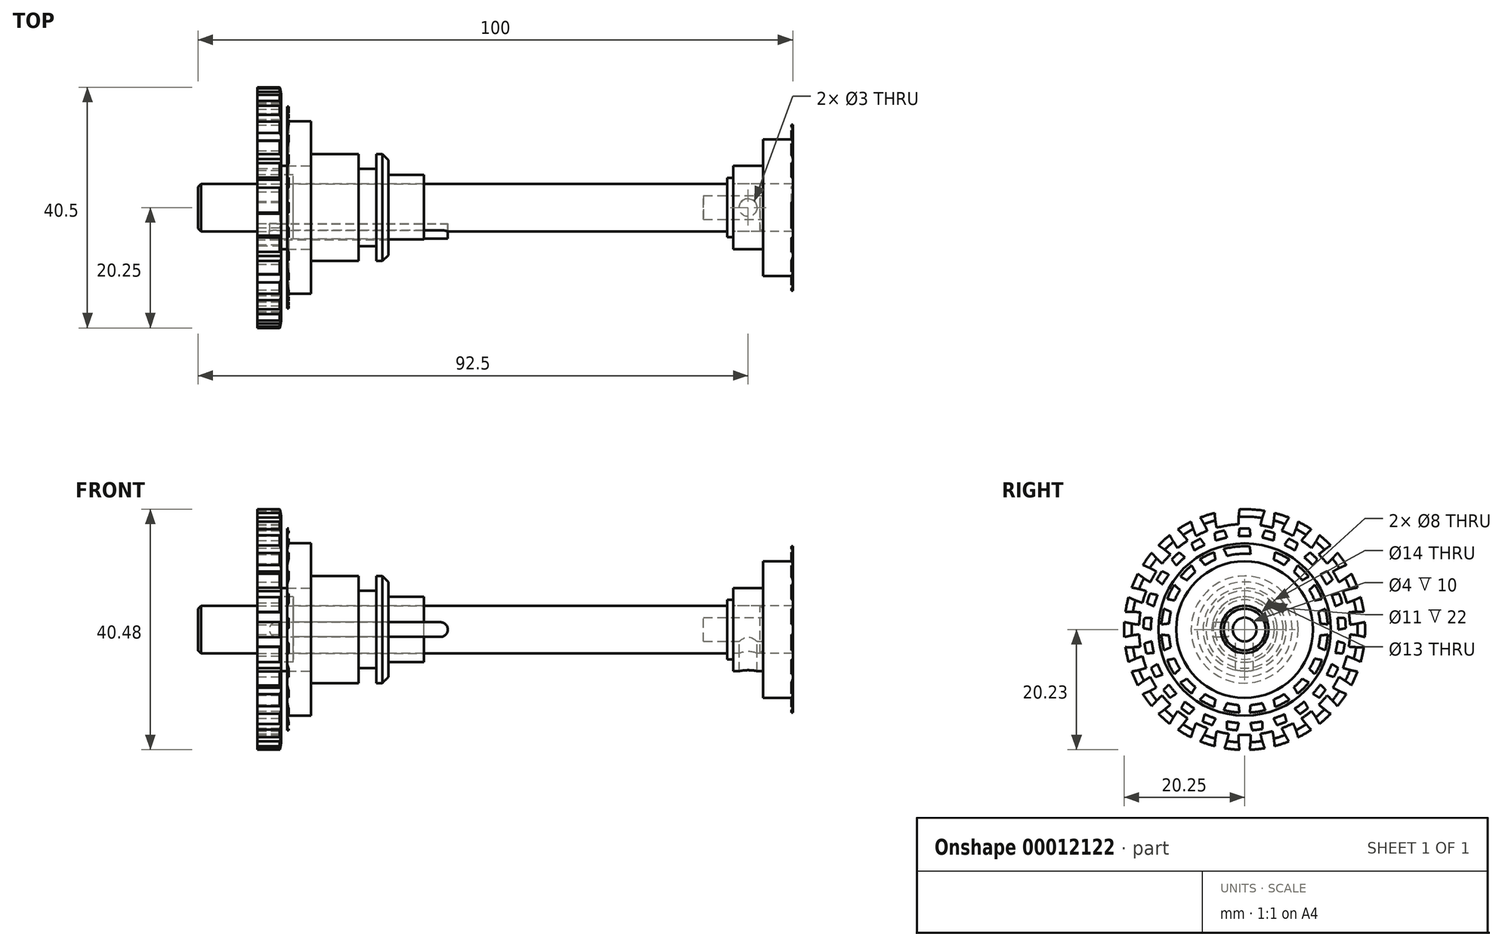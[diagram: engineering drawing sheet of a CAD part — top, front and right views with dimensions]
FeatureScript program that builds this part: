
annotation { "Feature Type Name" : "Feature", "Feature Type Description" : "" }
export const myFeature = defineFeature(function(context is Context, id is Id, definition is map)
    precondition{}
    {
        {
            var Q0;
            Q0=qCreatedBy(makeId("Right.planeOp"),FACE);
            var sketch = newSketch(context, id + "F0", { "sketchPlane" : qUnion([Q0])});
            skCircle(sketch, "E0", {"center": v(0, 0) * mm, "radius": 2 * mm});
            skCircle(sketch, "E1", {"center": v(0, 0) * mm, "radius": 4 * mm});
            skCircle(sketch, "E2", {"center": v(0, 0) * mm, "radius": 5 * mm});
            skSolve(sketch);
        }
        {
            var Q0;
            Q0=makeQuery(id+"F0.imprint","IMPRINT",FACE,{"disambiguationData":[TD([[makeQuery(id+"F0.imprint","IMPRINT",EDGE,{"derivedFrom":sQuery(id+"F0.wireOp",EDGE,"E0")}),-1.0]])]});
            var Q1;
            Q1=makeQuery(id+"F0.imprint","IMPRINT",FACE,{"disambiguationData":[TD([[makeQuery(id+"F0.imprint","IMPRINT",EDGE,{"derivedFrom":sQuery(id+"F0.wireOp",EDGE,"E0")}),1.0]])]});
            extrude(context, id + "F1", {"entities" : qUnion([Q0, Q1]), "oppositeDirection" : true, "depth" : 90 * mm});
        }
        {
            var Q0;
            Q0=makeQuery(id+"F0.imprint","IMPRINT",FACE,{"disambiguationData":[TD([[makeQuery(id+"F0.imprint","IMPRINT",EDGE,{"derivedFrom":sQuery(id+"F0.wireOp",EDGE,"E1")}),-1.0]])]});
            var Q1;
            Q1=makeQuery(id+"F0.imprint","IMPRINT",FACE,{"disambiguationData":[TD([[makeQuery(id+"F0.imprint","IMPRINT",EDGE,{"derivedFrom":sQuery(id+"F0.wireOp",EDGE,"E0")}),-1.0]])]});
            extrude(context, id + "F2", {"entities" : qUnion([Q0, Q1]), "operationType" : NewBodyOperationType.ADD, "oppositeDirection" : true, "depth" : 1 * mm});
        }
        {
            var Q0;
            Q0=makeQuery(id+"F0.imprint","IMPRINT",FACE,{"disambiguationData":[TD([[makeQuery(id+"F0.imprint","IMPRINT",EDGE,{"derivedFrom":sQuery(id+"F0.wireOp",EDGE,"E0")}),1.0]])]});
            extrude(context, id + "F3", {"entities" : qUnion([Q0]), "operationType" : NewBodyOperationType.REMOVE, "oppositeDirection" : true, "depth" : 5 * mm});
        }
        {
            var Q0;
            Q0=makeQuery(id+"F0.imprint","IMPRINT",FACE,{"disambiguationData":[TD([[makeQuery(id+"F0.imprint","IMPRINT",EDGE,{"derivedFrom":sQuery(id+"F0.wireOp",EDGE,"E0")}),-1.0]])]});
            extrude(context, id + "F4", {"entities" : qUnion([Q0]), "operationType" : NewBodyOperationType.ADD, "depth" : 5 * mm});
        }
        {
            var Q0;
            Q0=qCreatedBy(makeId("Front.planeOp"),FACE);
            cPlane(context, id + "F5", {"entities" : qUnion([Q0]), "cplaneType" : CPlaneType.OFFSET, "offset" : 4 * mm, "width" : 150 * mm, "height" : 150 * mm});
        }
        {
            var Q0;
            Q0=qCreatedBy(id+"F5.planeOp",FACE);
            var sketch = newSketch(context, id + "F6", { "sketchPlane" : qUnion([Q0])});
            skLineSegment(sketch, "E3.0", {"start": v(-90, 4) * mm, "end": v(-90, -4) * mm});
            skLineSegment(sketch, "E4", {"start": v(-90, 0) * mm, "end": v(-49.25, 0) * mm, "construction": true});
            skCircle(sketch, "E5", {"center": v(-49.25, 0) * mm, "radius": 1.25 * mm});
            skCircle(sketch, "E6", {"center": v(-76.75, 0) * mm, "radius": 1.25 * mm});
            skLineSegment(sketch, "E7", {"start": v(-76.75, 1.25) * mm, "end": v(-49.25, 1.25) * mm});
            skLineSegment(sketch, "E8", {"start": v(-76.75, -1.25) * mm, "end": v(-49.25, -1.25) * mm});
            skSolve(sketch);
        }
        {
            var Q0;
            {var subQ0=sQuery(id+"F6.wireOp",EDGE,"E6");var subQ2=makeQuery(id+"F6.imprint","INTERSECT",VERTEX,{"derivedFrom":[subQ0,sQuery(id+"F6.wireOp",EDGE,"E7")]});Q0=makeQuery(id+"F6.imprint","IMPRINT",FACE,{"disambiguationData":[TD([[makeQuery(id+"F6.imprint","IMPRINT",EDGE,{"disambiguationData":[TD([[subQ2,-1.0]])],"derivedFrom":subQ0}),1.0]])]});}
            var Q1;
            {var subQ1=sQuery(id+"F6.wireOp",EDGE,"E7");Q1=makeQuery(id+"F6.imprint","IMPRINT",FACE,{"disambiguationData":[TD([[makeQuery(id+"F6.imprint","IMPRINT",EDGE,{"derivedFrom":subQ1}),-1.0]])]});}
            var Q2;
            {var subQ0=sQuery(id+"F6.wireOp",EDGE,"E5");var subQ2=makeQuery(id+"F6.imprint","INTERSECT",VERTEX,{"derivedFrom":[subQ0,sQuery(id+"F6.wireOp",EDGE,"E7")]});Q2=makeQuery(id+"F6.imprint","IMPRINT",FACE,{"disambiguationData":[TD([[makeQuery(id+"F6.imprint","IMPRINT",EDGE,{"disambiguationData":[TD([[subQ2,-1.0]])],"derivedFrom":subQ0}),1.0]])]});}
            extrude(context, id + "F7", {"entities" : qUnion([Q0, Q1, Q2]), "operationType" : NewBodyOperationType.REMOVE, "oppositeDirection" : true, "depth" : 1.3 * mm});
        }
        {
            var Q0;
            {var subQ0=sQuery(id+"F6.wireOp",EDGE,"E6");var subQ2=makeQuery(id+"F6.imprint","INTERSECT",VERTEX,{"derivedFrom":[subQ0,sQuery(id+"F6.wireOp",EDGE,"E7")]});Q0=makeQuery(id+"F6.imprint","IMPRINT",FACE,{"disambiguationData":[TD([[makeQuery(id+"F6.imprint","IMPRINT",EDGE,{"disambiguationData":[TD([[subQ2,-1.0]])],"derivedFrom":subQ0}),1.0]])]});}
            var Q1;
            {var subQ1=sQuery(id+"F6.wireOp",EDGE,"E7");Q1=makeQuery(id+"F6.imprint","IMPRINT",FACE,{"disambiguationData":[TD([[makeQuery(id+"F6.imprint","IMPRINT",EDGE,{"derivedFrom":subQ1}),-1.0]])]});}
            var Q2;
            {var subQ0=sQuery(id+"F6.wireOp",EDGE,"E5");var subQ2=makeQuery(id+"F6.imprint","INTERSECT",VERTEX,{"derivedFrom":[subQ0,sQuery(id+"F6.wireOp",EDGE,"E7")]});Q2=makeQuery(id+"F6.imprint","IMPRINT",FACE,{"disambiguationData":[TD([[makeQuery(id+"F6.imprint","IMPRINT",EDGE,{"disambiguationData":[TD([[subQ2,-1.0]])],"derivedFrom":subQ0}),1.0]])]});}
            extrude(context, id + "F8", {"entities" : qUnion([Q0, Q1, Q2]), "depth" : 2.5 * mm, "symmetric" : true});
        }
        {
            var Q0;
            Q0=makeQuery(id+"F4.opExtrude","CAP_EDGE",EDGE,{"disambiguationData":[OSD([sQuery(id+"F0.wireOp",EDGE,"E1")])],"isStart":false});
            var Q1;
            Q1=makeQuery(id+"F1.opExtrude","CAP_EDGE",EDGE,{"disambiguationData":[OSD([sQuery(id+"F0.wireOp",EDGE,"E1")])],"isStart":false});
            chamfer(context, id + "F9", {"entities" : qUnion([Q0, Q1]), "width" : 0.5 * mm, "tangentPropagation" : true});
        }
        {
            var Q0;
            Q0=qCreatedBy(makeId("Right.planeOp"),FACE);
            cPlane(context, id + "F10", {"entities" : qUnion([Q0]), "cplaneType" : CPlaneType.OFFSET, "offset" : (48 + 15) * mm, "oppositeDirection" : true, "width" : 150 * mm, "height" : 150 * mm});
        }
        {
            var Q0;
            Q0=qCreatedBy(id+"F10.planeOp",FACE);
            var sketch = newSketch(context, id + "F11", { "sketchPlane" : qUnion([Q0])});
            skCircle(sketch, "E9.0", {"center": v(0, 0) * mm, "radius": 4 * mm});
            skLineSegment(sketch, "E9.1", {"start": v(-5.36, -1.25) * mm, "end": v(-2.75, -1.25) * mm});
            skLineSegment(sketch, "E9.2", {"start": v(-5.36, 1.25) * mm, "end": v(-2.75, 1.25) * mm});
            skCircle(sketch, "E10", {"center": v(0, 0) * mm, "radius": 5.5 * mm});
            skPoint(sketch, "E11.orphan", {"position": v(-5.25, 1.25) * mm});
            skPoint(sketch, "E12.orphan", {"position": v(-5.25, -1.25) * mm});
            skSolve(sketch);
        }
        {
            var Q0;
            {var subQ3=sQuery(id+"F11.wireOp",EDGE,"E9.1");var subQ5=sQuery(id+"F11.wireOp",EDGE,"E9.0");var subQ7=makeQuery(id+"F11.imprint","INTERSECT",VERTEX,{"derivedFrom":[subQ5,subQ3]});Q0=makeQuery(id+"F11.imprint","IMPRINT",FACE,{"disambiguationData":[TD([[makeQuery(id+"F11.imprint","IMPRINT",EDGE,{"disambiguationData":[TD([[subQ7,-1.0]])],"derivedFrom":subQ5}),-1.0]])]});}
            extrude(context, id + "F12", {"entities" : qUnion([Q0]), "depth" : 22 * mm, "symmetric" : true});
        }
        {
            var Q0;
            Q0=qCreatedBy(id+"F10.planeOp",FACE);
            var sketch = newSketch(context, id + "F13", { "sketchPlane" : qUnion([Q0])});
            skCircle(sketch, "E13.1", {"center": v(0, 0) * mm, "radius": 5.5 * mm});
            skCircle(sketch, "E14", {"center": v(0, 0) * mm, "radius": 6.5 * mm});
            skCircle(sketch, "E15", {"center": v(0, 0) * mm, "radius": 7 * mm});
            skCircle(sketch, "E16", {"center": v(0, 0) * mm, "radius": 9 * mm});
            skSolve(sketch);
        }
        {
            var Q0;
            Q0=makeQuery(id+"F13.imprint","IMPRINT",FACE,{"disambiguationData":[TD([[makeQuery(id+"F13.imprint","IMPRINT",EDGE,{"derivedFrom":sQuery(id+"F13.wireOp",EDGE,"E13.1")}),-1.0]])]});
            var Q1;
            Q1=makeQuery(id+"F13.imprint","IMPRINT",FACE,{"disambiguationData":[TD([[makeQuery(id+"F13.imprint","IMPRINT",EDGE,{"derivedFrom":sQuery(id+"F13.wireOp",EDGE,"E14")}),-1.0]])]});
            var Q2;
            Q2=makeQuery(id+"F13.imprint","IMPRINT",FACE,{"disambiguationData":[TD([[makeQuery(id+"F13.imprint","IMPRINT",EDGE,{"derivedFrom":sQuery(id+"F13.wireOp",EDGE,"E15")}),-1.0]])]});
            extrude(context, id + "F14", {"entities" : qUnion([Q0, Q1, Q2]), "depth" : 5 * mm});
        }
        {
            var Q0;
            Q0=makeQuery(id+"F13.imprint","IMPRINT",FACE,{"disambiguationData":[TD([[makeQuery(id+"F13.imprint","IMPRINT",EDGE,{"derivedFrom":sQuery(id+"F13.wireOp",EDGE,"E15")}),-1.0]])]});
            var Q1;
            Q1=makeQuery(id+"F13.imprint","IMPRINT",FACE,{"disambiguationData":[TD([[makeQuery(id+"F13.imprint","IMPRINT",EDGE,{"derivedFrom":sQuery(id+"F13.wireOp",EDGE,"E14")}),-1.0]])]});
            extrude(context, id + "F15", {"entities" : qUnion([Q0, Q1]), "operationType" : NewBodyOperationType.REMOVE, "depth" : 3 * mm});
        }
        {
            var Q0;
            Q0=makeQuery(id+"F13.imprint","IMPRINT",FACE,{"disambiguationData":[TD([[makeQuery(id+"F13.imprint","IMPRINT",EDGE,{"derivedFrom":sQuery(id+"F13.wireOp",EDGE,"E13.1")}),-1.0]])]});
            extrude(context, id + "F16", {"entities" : qUnion([Q0]), "operationType" : NewBodyOperationType.ADD, "oppositeDirection" : true, "depth" : (4 + 5 + 8) * mm});
        }
        {
            var Q0;
            Q0=makeQuery(id+"F13.imprint","IMPRINT",FACE,{"disambiguationData":[TD([[makeQuery(id+"F13.imprint","IMPRINT",EDGE,{"derivedFrom":sQuery(id+"F13.wireOp",EDGE,"E14")}),-1.0]])]});
            extrude(context, id + "F17", {"entities" : qUnion([Q0]), "operationType" : NewBodyOperationType.ADD, "oppositeDirection" : true, "depth" : (5 + 8) * mm});
        }
        {
            var Q0;
            Q0=makeQuery(id+"F13.imprint","IMPRINT",FACE,{"disambiguationData":[TD([[makeQuery(id+"F13.imprint","IMPRINT",EDGE,{"derivedFrom":sQuery(id+"F13.wireOp",EDGE,"E15")}),-1.0]])]});
            extrude(context, id + "F18", {"entities" : qUnion([Q0]), "operationType" : NewBodyOperationType.ADD, "oppositeDirection" : true, "depth" : 8 * mm});
        }
        {
            var Q0;
            Q0=makeQuery(id+"F14.opExtrude","CAP_EDGE",EDGE,{"disambiguationData":[OSD([sQuery(id+"F13.wireOp",EDGE,"E16")])],"isStart":false});
            chamfer(context, id + "F19", {"entities" : qUnion([Q0]), "width" : 1 * mm, "tangentPropagation" : true});
        }
        {
            var Q0;
            Q0=makeQuery(id+"F17.opExtrude","CAP_FACE",FACE,{"disambiguationData":[OSD([sQuery(id+"F13.wireOp",EDGE,"E14"),sQuery(id+"F13.wireOp",EDGE,"E15")])],"isStart":false});
            var sketch = newSketch(context, id + "F20", { "sketchPlane" : qUnion([Q0])});
            skCircle(sketch, "E17.0", {"center": v(0, 0) * mm, "radius": 6.5 * mm});
            skCircle(sketch, "E18", {"center": v(0, 0) * mm, "radius": 17.75 * mm});
            skCircle(sketch, "E19", {"center": v(0, 0) * mm, "radius": 20.25 * mm});
            skCircle(sketch, "E20", {"center": v(0, 0) * mm, "radius": 19 * mm, "construction": true});
            skLineSegment(sketch, "E21", {"start": v(0, 0) * mm, "end": v(0, 19) * mm, "construction": true});
            skLineSegment(sketch, "E22", {"start": v(0, 19) * mm, "end": v(0, 20.25) * mm, "construction": true});
            skLineSegment(sketch, "E23", {"start": v(0, 17.75) * mm, "end": v(15, 17.75) * mm, "construction": true});
            skLineSegment(sketch, "E24", {"start": v(0, 0) * mm, "end": v(-1, 18.97) * mm, "construction": true});
            skArc(sketch, "E25", {"start": v(-0.85, 20.23) * mm, "mid": v(-1, 18.98) * mm, "end": v(-1.04, 17.72) * mm});
            skArc(sketch, "E26.0.MirrorCS", {"start": v(0.85, 20.23) * mm, "mid": v(1, 18.98) * mm, "end": v(1.04, 17.72) * mm});
            skArc(sketch, "E27.1.0", {"start": v(-3.38, 19.97) * mm, "mid": v(-2.97, 18.77) * mm, "end": v(-2.67, 17.55) * mm});
            skArc(sketch, "E27.1.1", {"start": v(-5.04, 19.61) * mm, "mid": v(-4.92, 18.36) * mm, "end": v(-4.7, 17.12) * mm});
            skArc(sketch, "E27.2.0", {"start": v(-7.45, 18.83) * mm, "mid": v(-6.81, 17.74) * mm, "end": v(-6.26, 16.61) * mm});
            skArc(sketch, "E27.2.1", {"start": v(-9, 18.14) * mm, "mid": v(-8.63, 16.93) * mm, "end": v(-8.16, 15.76) * mm});
            skArc(sketch, "E27.3.0", {"start": v(-11.2, 16.87) * mm, "mid": v(-10.35, 15.94) * mm, "end": v(-9.57, 14.95) * mm});
            skArc(sketch, "E27.3.1", {"start": v(-12.58, 15.87) * mm, "mid": v(-11.96, 14.77) * mm, "end": v(-11.26, 13.72) * mm});
            skArc(sketch, "E27.4.0", {"start": v(-14.47, 14.17) * mm, "mid": v(-13.44, 13.44) * mm, "end": v(-12.47, 12.63) * mm});
            skArc(sketch, "E27.4.1", {"start": v(-15.6, 12.9) * mm, "mid": v(-14.77, 11.96) * mm, "end": v(-13.86, 11.08) * mm});
            skArc(sketch, "E27.5.0", {"start": v(-17.1, 10.85) * mm, "mid": v(-15.94, 10.35) * mm, "end": v(-14.82, 9.76) * mm});
            skArc(sketch, "E27.5.1", {"start": v(-17.95, 9.38) * mm, "mid": v(-16.93, 8.63) * mm, "end": v(-15.87, 7.96) * mm});
            skArc(sketch, "E27.6.0", {"start": v(-18.98, 7.06) * mm, "mid": v(-17.74, 6.81) * mm, "end": v(-16.53, 6.47) * mm});
            skArc(sketch, "E27.6.1", {"start": v(-19.5, 5.45) * mm, "mid": v(-18.36, 4.92) * mm, "end": v(-17.17, 4.49) * mm});
            skArc(sketch, "E27.7.0", {"start": v(-20.03, 2.96) * mm, "mid": v(-18.77, 2.97) * mm, "end": v(-17.51, 2.89) * mm});
            skArc(sketch, "E27.7.1", {"start": v(-20.21, 1.27) * mm, "mid": v(-18.98, 1) * mm, "end": v(-17.73, 0.82) * mm});
            skArc(sketch, "E27.8.0", {"start": v(-20.21, -1.27) * mm, "mid": v(-18.98, -1) * mm, "end": v(-17.73, -0.82) * mm});
            skArc(sketch, "E27.8.1", {"start": v(-20.03, -2.96) * mm, "mid": v(-18.77, -2.97) * mm, "end": v(-17.51, -2.89) * mm});
            skArc(sketch, "E27.9.0", {"start": v(-19.5, -5.45) * mm, "mid": v(-18.36, -4.92) * mm, "end": v(-17.17, -4.49) * mm});
            skArc(sketch, "E27.9.1", {"start": v(-18.98, -7.06) * mm, "mid": v(-17.74, -6.81) * mm, "end": v(-16.53, -6.47) * mm});
            skArc(sketch, "E27.10.0", {"start": v(-17.95, -9.38) * mm, "mid": v(-16.93, -8.63) * mm, "end": v(-15.87, -7.96) * mm});
            skArc(sketch, "E27.10.1", {"start": v(-17.1, -10.85) * mm, "mid": v(-15.94, -10.35) * mm, "end": v(-14.82, -9.76) * mm});
            skArc(sketch, "E27.11.0", {"start": v(-15.6, -12.9) * mm, "mid": v(-14.77, -11.96) * mm, "end": v(-13.86, -11.08) * mm});
            skArc(sketch, "E27.11.1", {"start": v(-14.47, -14.17) * mm, "mid": v(-13.44, -13.44) * mm, "end": v(-12.47, -12.63) * mm});
            skArc(sketch, "E27.12.0", {"start": v(-12.58, -15.87) * mm, "mid": v(-11.96, -14.77) * mm, "end": v(-11.26, -13.72) * mm});
            skArc(sketch, "E27.12.1", {"start": v(-11.2, -16.87) * mm, "mid": v(-10.35, -15.94) * mm, "end": v(-9.57, -14.95) * mm});
            skArc(sketch, "E27.13.0", {"start": v(-9, -18.14) * mm, "mid": v(-8.63, -16.93) * mm, "end": v(-8.16, -15.76) * mm});
            skArc(sketch, "E27.13.1", {"start": v(-7.45, -18.83) * mm, "mid": v(-6.81, -17.74) * mm, "end": v(-6.26, -16.61) * mm});
            skArc(sketch, "E27.14.0", {"start": v(-5.04, -19.61) * mm, "mid": v(-4.92, -18.36) * mm, "end": v(-4.7, -17.12) * mm});
            skArc(sketch, "E27.14.1", {"start": v(-3.38, -19.97) * mm, "mid": v(-2.97, -18.77) * mm, "end": v(-2.67, -17.55) * mm});
            skArc(sketch, "E27.15.0", {"start": v(-0.85, -20.23) * mm, "mid": v(-1, -18.98) * mm, "end": v(-1.04, -17.72) * mm});
            skArc(sketch, "E27.15.1", {"start": v(0.85, -20.23) * mm, "mid": v(1, -18.98) * mm, "end": v(1.04, -17.72) * mm});
            skArc(sketch, "E27.16.0", {"start": v(3.38, -19.97) * mm, "mid": v(2.97, -18.77) * mm, "end": v(2.67, -17.55) * mm});
            skArc(sketch, "E27.16.1", {"start": v(5.04, -19.61) * mm, "mid": v(4.92, -18.36) * mm, "end": v(4.7, -17.12) * mm});
            skArc(sketch, "E27.17.0", {"start": v(7.45, -18.83) * mm, "mid": v(6.81, -17.74) * mm, "end": v(6.26, -16.61) * mm});
            skArc(sketch, "E27.17.1", {"start": v(9, -18.14) * mm, "mid": v(8.63, -16.93) * mm, "end": v(8.16, -15.76) * mm});
            skArc(sketch, "E27.18.0", {"start": v(11.2, -16.87) * mm, "mid": v(10.35, -15.94) * mm, "end": v(9.57, -14.95) * mm});
            skArc(sketch, "E27.18.1", {"start": v(12.58, -15.87) * mm, "mid": v(11.96, -14.77) * mm, "end": v(11.26, -13.72) * mm});
            skArc(sketch, "E27.19.0", {"start": v(14.47, -14.17) * mm, "mid": v(13.44, -13.44) * mm, "end": v(12.47, -12.63) * mm});
            skArc(sketch, "E27.19.1", {"start": v(15.6, -12.9) * mm, "mid": v(14.77, -11.96) * mm, "end": v(13.86, -11.08) * mm});
            skArc(sketch, "E27.20.0", {"start": v(17.1, -10.85) * mm, "mid": v(15.94, -10.35) * mm, "end": v(14.82, -9.76) * mm});
            skArc(sketch, "E27.20.1", {"start": v(17.95, -9.38) * mm, "mid": v(16.93, -8.63) * mm, "end": v(15.87, -7.96) * mm});
            skArc(sketch, "E27.21.0", {"start": v(18.98, -7.06) * mm, "mid": v(17.74, -6.81) * mm, "end": v(16.53, -6.47) * mm});
            skArc(sketch, "E27.21.1", {"start": v(19.5, -5.45) * mm, "mid": v(18.36, -4.92) * mm, "end": v(17.17, -4.49) * mm});
            skArc(sketch, "E27.22.0", {"start": v(20.03, -2.96) * mm, "mid": v(18.77, -2.97) * mm, "end": v(17.51, -2.89) * mm});
            skArc(sketch, "E27.22.1", {"start": v(20.21, -1.27) * mm, "mid": v(18.98, -1) * mm, "end": v(17.73, -0.82) * mm});
            skArc(sketch, "E27.23.0", {"start": v(20.21, 1.27) * mm, "mid": v(18.98, 1) * mm, "end": v(17.73, 0.82) * mm});
            skArc(sketch, "E27.23.1", {"start": v(20.03, 2.96) * mm, "mid": v(18.77, 2.97) * mm, "end": v(17.51, 2.89) * mm});
            skArc(sketch, "E27.24.0", {"start": v(19.5, 5.45) * mm, "mid": v(18.36, 4.92) * mm, "end": v(17.17, 4.49) * mm});
            skArc(sketch, "E27.24.1", {"start": v(18.98, 7.06) * mm, "mid": v(17.74, 6.81) * mm, "end": v(16.53, 6.47) * mm});
            skArc(sketch, "E27.25.0", {"start": v(17.95, 9.38) * mm, "mid": v(16.93, 8.63) * mm, "end": v(15.87, 7.96) * mm});
            skArc(sketch, "E27.25.1", {"start": v(17.1, 10.85) * mm, "mid": v(15.94, 10.35) * mm, "end": v(14.82, 9.76) * mm});
            skArc(sketch, "E27.26.0", {"start": v(15.6, 12.9) * mm, "mid": v(14.77, 11.96) * mm, "end": v(13.86, 11.08) * mm});
            skArc(sketch, "E27.26.1", {"start": v(14.47, 14.17) * mm, "mid": v(13.44, 13.44) * mm, "end": v(12.47, 12.63) * mm});
            skArc(sketch, "E27.27.0", {"start": v(12.58, 15.87) * mm, "mid": v(11.96, 14.77) * mm, "end": v(11.26, 13.72) * mm});
            skArc(sketch, "E27.27.1", {"start": v(11.2, 16.87) * mm, "mid": v(10.35, 15.94) * mm, "end": v(9.57, 14.95) * mm});
            skArc(sketch, "E27.28.0", {"start": v(9, 18.14) * mm, "mid": v(8.63, 16.93) * mm, "end": v(8.16, 15.76) * mm});
            skArc(sketch, "E27.28.1", {"start": v(7.45, 18.83) * mm, "mid": v(6.81, 17.74) * mm, "end": v(6.26, 16.61) * mm});
            skArc(sketch, "E27.29.0", {"start": v(5.04, 19.61) * mm, "mid": v(4.92, 18.36) * mm, "end": v(4.7, 17.12) * mm});
            skArc(sketch, "E27.29.1", {"start": v(3.38, 19.97) * mm, "mid": v(2.97, 18.77) * mm, "end": v(2.67, 17.55) * mm});
            skSolve(sketch);
        }
        {
            var Q0;
            Q0=makeQuery(id+"F20.imprint","IMPRINT",FACE,{"disambiguationData":[TD([[makeQuery(id+"F20.imprint","IMPRINT",EDGE,{"derivedFrom":makeQuery(id+"F17.opExtrude","CAP_EDGE",EDGE,{"disambiguationData":[OSD([sQuery(id+"F13.wireOp",EDGE,"E15")])],"isStart":false})}),1.0]])]});
            var Q1;
            Q1=makeQuery(id+"F20.imprint","IMPRINT",FACE,{"disambiguationData":[TD([[makeQuery(id+"F20.imprint","IMPRINT",EDGE,{"derivedFrom":sQuery(id+"F20.wireOp",EDGE,"E17.0")}),1.0]])]});
            var Q2;
            {var subQ1=sQuery(id+"F20.wireOp",EDGE,"E25");Q2=makeQuery(id+"F20.imprint","IMPRINT",FACE,{"disambiguationData":[TD([[makeQuery(id+"F20.imprint","IMPRINT",EDGE,{"derivedFrom":subQ1}),1.0]])]});}
            var Q3;
            {var subQ1=sQuery(id+"F20.wireOp",EDGE,"E27.1.0");Q3=makeQuery(id+"F20.imprint","IMPRINT",FACE,{"disambiguationData":[TD([[makeQuery(id+"F20.imprint","IMPRINT",EDGE,{"derivedFrom":subQ1}),-1.0]])]});}
            var Q4;
            {var subQ1=sQuery(id+"F20.wireOp",EDGE,"E27.2.0");Q4=makeQuery(id+"F20.imprint","IMPRINT",FACE,{"disambiguationData":[TD([[makeQuery(id+"F20.imprint","IMPRINT",EDGE,{"derivedFrom":subQ1}),-1.0]])]});}
            var Q5;
            {var subQ1=sQuery(id+"F20.wireOp",EDGE,"E27.3.0");Q5=makeQuery(id+"F20.imprint","IMPRINT",FACE,{"disambiguationData":[TD([[makeQuery(id+"F20.imprint","IMPRINT",EDGE,{"derivedFrom":subQ1}),-1.0]])]});}
            var Q6;
            {var subQ1=sQuery(id+"F20.wireOp",EDGE,"E27.4.0");Q6=makeQuery(id+"F20.imprint","IMPRINT",FACE,{"disambiguationData":[TD([[makeQuery(id+"F20.imprint","IMPRINT",EDGE,{"derivedFrom":subQ1}),-1.0]])]});}
            var Q7;
            {var subQ1=sQuery(id+"F20.wireOp",EDGE,"E27.5.0");Q7=makeQuery(id+"F20.imprint","IMPRINT",FACE,{"disambiguationData":[TD([[makeQuery(id+"F20.imprint","IMPRINT",EDGE,{"derivedFrom":subQ1}),-1.0]])]});}
            var Q8;
            {var subQ1=sQuery(id+"F20.wireOp",EDGE,"E27.6.0");Q8=makeQuery(id+"F20.imprint","IMPRINT",FACE,{"disambiguationData":[TD([[makeQuery(id+"F20.imprint","IMPRINT",EDGE,{"derivedFrom":subQ1}),-1.0]])]});}
            var Q9;
            {var subQ1=sQuery(id+"F20.wireOp",EDGE,"E27.7.0");Q9=makeQuery(id+"F20.imprint","IMPRINT",FACE,{"disambiguationData":[TD([[makeQuery(id+"F20.imprint","IMPRINT",EDGE,{"derivedFrom":subQ1}),-1.0]])]});}
            var Q10;
            {var subQ1=sQuery(id+"F20.wireOp",EDGE,"E27.8.0");Q10=makeQuery(id+"F20.imprint","IMPRINT",FACE,{"disambiguationData":[TD([[makeQuery(id+"F20.imprint","IMPRINT",EDGE,{"derivedFrom":subQ1}),-1.0]])]});}
            var Q11;
            {var subQ1=sQuery(id+"F20.wireOp",EDGE,"E27.9.0");Q11=makeQuery(id+"F20.imprint","IMPRINT",FACE,{"disambiguationData":[TD([[makeQuery(id+"F20.imprint","IMPRINT",EDGE,{"derivedFrom":subQ1}),-1.0]])]});}
            var Q12;
            {var subQ1=sQuery(id+"F20.wireOp",EDGE,"E27.10.0");Q12=makeQuery(id+"F20.imprint","IMPRINT",FACE,{"disambiguationData":[TD([[makeQuery(id+"F20.imprint","IMPRINT",EDGE,{"derivedFrom":subQ1}),-1.0]])]});}
            var Q13;
            {var subQ1=sQuery(id+"F20.wireOp",EDGE,"E27.11.0");Q13=makeQuery(id+"F20.imprint","IMPRINT",FACE,{"disambiguationData":[TD([[makeQuery(id+"F20.imprint","IMPRINT",EDGE,{"derivedFrom":subQ1}),-1.0]])]});}
            var Q14;
            {var subQ1=sQuery(id+"F20.wireOp",EDGE,"E27.12.0");Q14=makeQuery(id+"F20.imprint","IMPRINT",FACE,{"disambiguationData":[TD([[makeQuery(id+"F20.imprint","IMPRINT",EDGE,{"derivedFrom":subQ1}),-1.0]])]});}
            var Q15;
            {var subQ1=sQuery(id+"F20.wireOp",EDGE,"E27.14.0");Q15=makeQuery(id+"F20.imprint","IMPRINT",FACE,{"disambiguationData":[TD([[makeQuery(id+"F20.imprint","IMPRINT",EDGE,{"derivedFrom":subQ1}),-1.0]])]});}
            var Q16;
            {var subQ2=sQuery(id+"F20.wireOp",EDGE,"E27.15.0");Q16=makeQuery(id+"F20.imprint","IMPRINT",FACE,{"disambiguationData":[TD([[makeQuery(id+"F20.imprint","IMPRINT",EDGE,{"derivedFrom":subQ2}),-1.0]])]});}
            var Q17;
            {var subQ1=sQuery(id+"F20.wireOp",EDGE,"E27.13.0");Q17=makeQuery(id+"F20.imprint","IMPRINT",FACE,{"disambiguationData":[TD([[makeQuery(id+"F20.imprint","IMPRINT",EDGE,{"derivedFrom":subQ1}),-1.0]])]});}
            var Q18;
            {var subQ2=sQuery(id+"F20.wireOp",EDGE,"E27.16.0");Q18=makeQuery(id+"F20.imprint","IMPRINT",FACE,{"disambiguationData":[TD([[makeQuery(id+"F20.imprint","IMPRINT",EDGE,{"derivedFrom":subQ2}),-1.0]])]});}
            var Q19;
            {var subQ1=sQuery(id+"F20.wireOp",EDGE,"E27.17.0");Q19=makeQuery(id+"F20.imprint","IMPRINT",FACE,{"disambiguationData":[TD([[makeQuery(id+"F20.imprint","IMPRINT",EDGE,{"derivedFrom":subQ1}),-1.0]])]});}
            var Q20;
            {var subQ1=sQuery(id+"F20.wireOp",EDGE,"E27.18.0");Q20=makeQuery(id+"F20.imprint","IMPRINT",FACE,{"disambiguationData":[TD([[makeQuery(id+"F20.imprint","IMPRINT",EDGE,{"derivedFrom":subQ1}),-1.0]])]});}
            var Q21;
            {var subQ1=sQuery(id+"F20.wireOp",EDGE,"E27.19.0");Q21=makeQuery(id+"F20.imprint","IMPRINT",FACE,{"disambiguationData":[TD([[makeQuery(id+"F20.imprint","IMPRINT",EDGE,{"derivedFrom":subQ1}),-1.0]])]});}
            var Q22;
            {var subQ1=sQuery(id+"F20.wireOp",EDGE,"E27.20.0");Q22=makeQuery(id+"F20.imprint","IMPRINT",FACE,{"disambiguationData":[TD([[makeQuery(id+"F20.imprint","IMPRINT",EDGE,{"derivedFrom":subQ1}),-1.0]])]});}
            var Q23;
            {var subQ1=sQuery(id+"F20.wireOp",EDGE,"E27.21.0");Q23=makeQuery(id+"F20.imprint","IMPRINT",FACE,{"disambiguationData":[TD([[makeQuery(id+"F20.imprint","IMPRINT",EDGE,{"derivedFrom":subQ1}),-1.0]])]});}
            var Q24;
            {var subQ1=sQuery(id+"F20.wireOp",EDGE,"E27.22.0");Q24=makeQuery(id+"F20.imprint","IMPRINT",FACE,{"disambiguationData":[TD([[makeQuery(id+"F20.imprint","IMPRINT",EDGE,{"derivedFrom":subQ1}),-1.0]])]});}
            var Q25;
            {var subQ1=sQuery(id+"F20.wireOp",EDGE,"E27.23.0");Q25=makeQuery(id+"F20.imprint","IMPRINT",FACE,{"disambiguationData":[TD([[makeQuery(id+"F20.imprint","IMPRINT",EDGE,{"derivedFrom":subQ1}),-1.0]])]});}
            var Q26;
            {var subQ1=sQuery(id+"F20.wireOp",EDGE,"E27.24.0");Q26=makeQuery(id+"F20.imprint","IMPRINT",FACE,{"disambiguationData":[TD([[makeQuery(id+"F20.imprint","IMPRINT",EDGE,{"derivedFrom":subQ1}),-1.0]])]});}
            var Q27;
            {var subQ1=sQuery(id+"F20.wireOp",EDGE,"E27.25.0");Q27=makeQuery(id+"F20.imprint","IMPRINT",FACE,{"disambiguationData":[TD([[makeQuery(id+"F20.imprint","IMPRINT",EDGE,{"derivedFrom":subQ1}),-1.0]])]});}
            var Q28;
            {var subQ1=sQuery(id+"F20.wireOp",EDGE,"E27.26.0");Q28=makeQuery(id+"F20.imprint","IMPRINT",FACE,{"disambiguationData":[TD([[makeQuery(id+"F20.imprint","IMPRINT",EDGE,{"derivedFrom":subQ1}),-1.0]])]});}
            var Q29;
            {var subQ1=sQuery(id+"F20.wireOp",EDGE,"E27.27.0");Q29=makeQuery(id+"F20.imprint","IMPRINT",FACE,{"disambiguationData":[TD([[makeQuery(id+"F20.imprint","IMPRINT",EDGE,{"derivedFrom":subQ1}),-1.0]])]});}
            var Q30;
            {var subQ1=sQuery(id+"F20.wireOp",EDGE,"E27.28.0");Q30=makeQuery(id+"F20.imprint","IMPRINT",FACE,{"disambiguationData":[TD([[makeQuery(id+"F20.imprint","IMPRINT",EDGE,{"derivedFrom":subQ1}),-1.0]])]});}
            var Q31;
            {var subQ1=sQuery(id+"F20.wireOp",EDGE,"E27.29.0");Q31=makeQuery(id+"F20.imprint","IMPRINT",FACE,{"disambiguationData":[TD([[makeQuery(id+"F20.imprint","IMPRINT",EDGE,{"derivedFrom":subQ1}),-1.0]])]});}
            extrude(context, id + "F21", {"entities" : qUnion([Q0, Q1, Q2, Q3, Q4, Q5, Q6, Q7, Q8, Q9, Q10, Q11, Q12, Q13, Q14, Q15, Q16, Q17, Q18, Q19, Q20, Q21, Q22, Q23, Q24, Q25, Q26, Q27, Q28, Q29, Q30, Q31]), "depth" : 4 * mm});
        }
        {
            var Q0;
            Q0=qCreatedBy(makeId("Front.planeOp"),FACE);
            var sketch = newSketch(context, id + "F22", { "sketchPlane" : qUnion([Q0])});
            skLineSegment(sketch, "E28.0", {"start": v(-76, -20.25) * mm, "end": v(-76, 20.25) * mm});
            skLineSegment(sketch, "E28.1", {"start": v(-76, -17.75) * mm, "end": v(-76, 17.75) * mm});
            skLineSegment(sketch, "E28.2", {"start": v(-76, -19) * mm, "end": v(-76, 19) * mm});
            skLineSegment(sketch, "E29", {"start": v(-76, 20.25) * mm, "end": v(-80, 20.25) * mm});
            skLineSegment(sketch, "E30", {"start": v(-80, 20.25) * mm, "end": v(-80, 17.75) * mm});
            skLineSegment(sketch, "E31", {"start": v(-76, 19) * mm, "end": v(-80, 19) * mm, "construction": true});
            skLineSegment(sketch, "E32", {"start": v(-78, 20.25) * mm, "end": v(-78, 19) * mm, "construction": true});
            skLineSegment(sketch, "E33", {"start": v(-76, 0) * mm, "end": v(-86.77, 0) * mm, "construction": true});
            skLineSegment(sketch, "E34", {"start": v(-76, 17.75) * mm, "end": v(-86, 17.75) * mm, "construction": true});
            skArc(sketch, "E35", {"start": v(-76, 19) * mm, "mid": v(-76.1, 19.63) * mm, "end": v(-76.24, 20.25) * mm});
            skArc(sketch, "E36.0.MirrorCS", {"start": v(-80, 19) * mm, "mid": v(-79.9, 19.63) * mm, "end": v(-79.76, 20.25) * mm});
            skSolve(sketch);
        }
        {
            var Q0;
            {var subQ0=sQuery(id+"F22.wireOp",EDGE,"E35");Q0=makeQuery(id+"F22.imprint","IMPRINT",FACE,{"disambiguationData":[TD([[makeQuery(id+"F22.imprint","IMPRINT",EDGE,{"derivedFrom":subQ0}),-1.0]])]});}
            var Q1;
            {var subQ0=sQuery(id+"F22.wireOp",EDGE,"E36.0.MirrorCS");Q1=makeQuery(id+"F22.imprint","IMPRINT",FACE,{"disambiguationData":[TD([[makeQuery(id+"F22.imprint","IMPRINT",EDGE,{"derivedFrom":subQ0}),1.0]])]});}
            var Q2;
            Q2=sQuery(id+"F22.wireOp",EDGE,"E33");
            revolve(context, id + "F23", {"operationType" : NewBodyOperationType.REMOVE, "entities" : qUnion([Q0, Q1]), "axis" : qUnion([Q2]), "revolveType" : RevolveType.FULL, "oppositeDirection" : true});
        }
        {
            var Q0;
            Q0=makeQuery(id+"F18.opExtrude","CAP_FACE",FACE,{"disambiguationData":[OSD([sQuery(id+"F13.wireOp",EDGE,"E15"),sQuery(id+"F13.wireOp",EDGE,"E16")])],"isStart":false});
            var sketch = newSketch(context, id + "F24", { "sketchPlane" : qUnion([Q0])});
            skCircle(sketch, "E37", {"center": v(0, 0) * mm, "radius": 14.5 * mm});
            skCircle(sketch, "E38", {"center": v(0, 0) * mm, "radius": 17 * mm});
            skCircle(sketch, "E39", {"center": v(0, 0) * mm, "radius": 15.75 * mm, "construction": true});
            skLineSegment(sketch, "E40", {"start": v(0, 0) * mm, "end": v(0, 17) * mm, "construction": true});
            skLineSegment(sketch, "E41", {"start": v(0, 0) * mm, "end": v(-0.99, 15.72) * mm, "construction": true});
            skLineSegment(sketch, "E42", {"start": v(0, 14.5) * mm, "end": v(15, 14.5) * mm, "construction": true});
            skArc(sketch, "E43", {"start": v(-0.84, 16.98) * mm, "mid": v(-0.99, 15.72) * mm, "end": v(-1.04, 14.46) * mm});
            skArc(sketch, "E44.0.MirrorCS", {"start": v(0.84, 16.98) * mm, "mid": v(0.99, 15.72) * mm, "end": v(1.04, 14.46) * mm});
            skArc(sketch, "E45.1.0", {"start": v(-5.04, 16.24) * mm, "mid": v(-4.87, 14.98) * mm, "end": v(-4.6, 13.75) * mm});
            skArc(sketch, "E45.1.1", {"start": v(-3.4, 16.66) * mm, "mid": v(-2.95, 15.48) * mm, "end": v(-2.6, 14.27) * mm});
            skArc(sketch, "E45.2.0", {"start": v(-8.92, 14.47) * mm, "mid": v(-8.44, 13.3) * mm, "end": v(-7.87, 12.18) * mm});
            skArc(sketch, "E45.2.1", {"start": v(-7.44, 15.28) * mm, "mid": v(-6.7, 14.26) * mm, "end": v(-6.06, 13.17) * mm});
            skArc(sketch, "E45.3.0", {"start": v(-12.24, 11.8) * mm, "mid": v(-11.48, 10.79) * mm, "end": v(-10.66, 9.83) * mm});
            skArc(sketch, "E45.3.1", {"start": v(-11, 12.95) * mm, "mid": v(-10.04, 12.14) * mm, "end": v(-9.15, 11.25) * mm});
            skArc(sketch, "E45.4.0", {"start": v(-14.79, 8.39) * mm, "mid": v(-13.8, 7.6) * mm, "end": v(-12.77, 6.88) * mm});
            skArc(sketch, "E45.4.1", {"start": v(-13.88, 9.8) * mm, "mid": v(-12.75, 9.26) * mm, "end": v(-11.66, 8.62) * mm});
            skArc(sketch, "E45.5.0", {"start": v(-16.4, 4.45) * mm, "mid": v(-15.26, 3.92) * mm, "end": v(-14.08, 3.48) * mm});
            skArc(sketch, "E45.5.1", {"start": v(-15.89, 6.05) * mm, "mid": v(-14.65, 5.8) * mm, "end": v(-13.44, 5.45) * mm});
            skArc(sketch, "E45.6.0", {"start": v(-17, 0.23) * mm, "mid": v(-15.76, 0) * mm, "end": v(-14.5, -0.13) * mm});
            skArc(sketch, "E45.6.1", {"start": v(-16.9, 1.9) * mm, "mid": v(-15.63, 1.97) * mm, "end": v(-14.37, 1.94) * mm});
            skArc(sketch, "E45.7.0", {"start": v(-16.52, -4) * mm, "mid": v(-15.26, -3.92) * mm, "end": v(-14.01, -3.73) * mm});
            skArc(sketch, "E45.7.1", {"start": v(-16.84, -2.35) * mm, "mid": v(-15.63, -1.98) * mm, "end": v(-14.4, -1.7) * mm});
            skArc(sketch, "E45.8.0", {"start": v(-15, -8) * mm, "mid": v(-13.8, -7.59) * mm, "end": v(-12.65, -7.1) * mm});
            skArc(sketch, "E45.8.1", {"start": v(-15.72, -6.47) * mm, "mid": v(-14.65, -5.8) * mm, "end": v(-13.53, -5.22) * mm});
            skArc(sketch, "E45.9.0", {"start": v(-12.55, -11.47) * mm, "mid": v(-11.49, -10.79) * mm, "end": v(-10.48, -10.02) * mm});
            skArc(sketch, "E45.9.1", {"start": v(-13.62, -10.17) * mm, "mid": v(-12.75, -9.26) * mm, "end": v(-11.8, -8.42) * mm});
            skArc(sketch, "E45.10.0", {"start": v(-9.3, -14.23) * mm, "mid": v(-8.44, -13.3) * mm, "end": v(-7.66, -12.3) * mm});
            skArc(sketch, "E45.10.1", {"start": v(-10.66, -13.24) * mm, "mid": v(-10.04, -12.14) * mm, "end": v(-9.34, -11.1) * mm});
            skArc(sketch, "E45.11.0", {"start": v(-5.47, -16.1) * mm, "mid": v(-4.87, -14.98) * mm, "end": v(-4.36, -13.83) * mm});
            skArc(sketch, "E45.11.1", {"start": v(-7.03, -15.48) * mm, "mid": v(-6.7, -14.26) * mm, "end": v(-6.29, -13.07) * mm});
            skArc(sketch, "E45.12.0", {"start": v(-1.3, -16.95) * mm, "mid": v(-1, -15.72) * mm, "end": v(-0.79, -14.48) * mm});
            skArc(sketch, "E45.12.1", {"start": v(-2.96, -16.74) * mm, "mid": v(-2.95, -15.48) * mm, "end": v(-2.84, -14.22) * mm});
            skArc(sketch, "E45.13.0", {"start": v(2.96, -16.74) * mm, "mid": v(2.95, -15.48) * mm, "end": v(2.84, -14.22) * mm});
            skArc(sketch, "E45.13.1", {"start": v(1.3, -16.95) * mm, "mid": v(1, -15.72) * mm, "end": v(0.79, -14.48) * mm});
            skArc(sketch, "E45.14.0", {"start": v(7.03, -15.48) * mm, "mid": v(6.7, -14.26) * mm, "end": v(6.29, -13.07) * mm});
            skArc(sketch, "E45.14.1", {"start": v(5.47, -16.1) * mm, "mid": v(4.87, -14.98) * mm, "end": v(4.36, -13.83) * mm});
            skArc(sketch, "E45.15.0", {"start": v(10.66, -13.24) * mm, "mid": v(10.04, -12.14) * mm, "end": v(9.34, -11.1) * mm});
            skArc(sketch, "E45.15.1", {"start": v(9.3, -14.23) * mm, "mid": v(8.44, -13.3) * mm, "end": v(7.66, -12.3) * mm});
            skArc(sketch, "E45.16.0", {"start": v(13.62, -10.17) * mm, "mid": v(12.75, -9.26) * mm, "end": v(11.8, -8.42) * mm});
            skArc(sketch, "E45.16.1", {"start": v(12.55, -11.47) * mm, "mid": v(11.49, -10.79) * mm, "end": v(10.48, -10.02) * mm});
            skArc(sketch, "E45.17.0", {"start": v(15.72, -6.47) * mm, "mid": v(14.65, -5.8) * mm, "end": v(13.53, -5.22) * mm});
            skArc(sketch, "E45.17.1", {"start": v(15, -8) * mm, "mid": v(13.8, -7.59) * mm, "end": v(12.65, -7.1) * mm});
            skArc(sketch, "E45.18.0", {"start": v(16.84, -2.35) * mm, "mid": v(15.63, -1.98) * mm, "end": v(14.4, -1.7) * mm});
            skArc(sketch, "E45.18.1", {"start": v(16.52, -4) * mm, "mid": v(15.26, -3.92) * mm, "end": v(14.01, -3.73) * mm});
            skArc(sketch, "E45.19.0", {"start": v(16.9, 1.9) * mm, "mid": v(15.63, 1.97) * mm, "end": v(14.37, 1.94) * mm});
            skArc(sketch, "E45.19.1", {"start": v(17, 0.23) * mm, "mid": v(15.76, 0) * mm, "end": v(14.5, -0.13) * mm});
            skArc(sketch, "E45.20.0", {"start": v(15.89, 6.05) * mm, "mid": v(14.65, 5.8) * mm, "end": v(13.44, 5.45) * mm});
            skArc(sketch, "E45.20.1", {"start": v(16.4, 4.45) * mm, "mid": v(15.26, 3.92) * mm, "end": v(14.08, 3.48) * mm});
            skArc(sketch, "E45.21.0", {"start": v(13.88, 9.8) * mm, "mid": v(12.75, 9.26) * mm, "end": v(11.66, 8.62) * mm});
            skArc(sketch, "E45.21.1", {"start": v(14.79, 8.39) * mm, "mid": v(13.8, 7.6) * mm, "end": v(12.77, 6.88) * mm});
            skArc(sketch, "E45.22.0", {"start": v(11, 12.95) * mm, "mid": v(10.04, 12.14) * mm, "end": v(9.15, 11.25) * mm});
            skArc(sketch, "E45.22.1", {"start": v(12.24, 11.8) * mm, "mid": v(11.48, 10.79) * mm, "end": v(10.66, 9.83) * mm});
            skArc(sketch, "E45.23.0", {"start": v(7.44, 15.28) * mm, "mid": v(6.7, 14.26) * mm, "end": v(6.06, 13.17) * mm});
            skArc(sketch, "E45.23.1", {"start": v(8.92, 14.47) * mm, "mid": v(8.44, 13.3) * mm, "end": v(7.87, 12.18) * mm});
            skArc(sketch, "E45.24.0", {"start": v(3.4, 16.66) * mm, "mid": v(2.95, 15.48) * mm, "end": v(2.6, 14.27) * mm});
            skArc(sketch, "E45.24.1", {"start": v(5.04, 16.24) * mm, "mid": v(4.87, 14.98) * mm, "end": v(4.6, 13.75) * mm});
            skSolve(sketch);
        }
        {
            var Q0;
            Q0=makeQuery(id+"F24.imprint","IMPRINT",FACE,{"disambiguationData":[TD([[makeQuery(id+"F24.imprint","IMPRINT",EDGE,{"derivedFrom":makeQuery(id+"F18.opExtrude","CAP_EDGE",EDGE,{"disambiguationData":[OSD([sQuery(id+"F13.wireOp",EDGE,"E16")])],"isStart":false})}),1.0]])]});
            var Q1;
            {var subQ1=sQuery(id+"F24.wireOp",EDGE,"E45.1.0");Q1=makeQuery(id+"F24.imprint","IMPRINT",FACE,{"disambiguationData":[TD([[makeQuery(id+"F24.imprint","IMPRINT",EDGE,{"derivedFrom":subQ1}),1.0]])]});}
            var Q2;
            {var subQ1=sQuery(id+"F24.wireOp",EDGE,"E43");Q2=makeQuery(id+"F24.imprint","IMPRINT",FACE,{"disambiguationData":[TD([[makeQuery(id+"F24.imprint","IMPRINT",EDGE,{"derivedFrom":subQ1}),1.0]])]});}
            var Q3;
            {var subQ1=sQuery(id+"F24.wireOp",EDGE,"E45.24.0");Q3=makeQuery(id+"F24.imprint","IMPRINT",FACE,{"disambiguationData":[TD([[makeQuery(id+"F24.imprint","IMPRINT",EDGE,{"derivedFrom":subQ1}),1.0]])]});}
            var Q4;
            {var subQ1=sQuery(id+"F24.wireOp",EDGE,"E45.23.0");Q4=makeQuery(id+"F24.imprint","IMPRINT",FACE,{"disambiguationData":[TD([[makeQuery(id+"F24.imprint","IMPRINT",EDGE,{"derivedFrom":subQ1}),1.0]])]});}
            var Q5;
            {var subQ1=sQuery(id+"F24.wireOp",EDGE,"E45.22.0");Q5=makeQuery(id+"F24.imprint","IMPRINT",FACE,{"disambiguationData":[TD([[makeQuery(id+"F24.imprint","IMPRINT",EDGE,{"derivedFrom":subQ1}),1.0]])]});}
            var Q6;
            {var subQ1=sQuery(id+"F24.wireOp",EDGE,"E45.21.0");Q6=makeQuery(id+"F24.imprint","IMPRINT",FACE,{"disambiguationData":[TD([[makeQuery(id+"F24.imprint","IMPRINT",EDGE,{"derivedFrom":subQ1}),1.0]])]});}
            var Q7;
            {var subQ1=sQuery(id+"F24.wireOp",EDGE,"E45.20.0");Q7=makeQuery(id+"F24.imprint","IMPRINT",FACE,{"disambiguationData":[TD([[makeQuery(id+"F24.imprint","IMPRINT",EDGE,{"derivedFrom":subQ1}),1.0]])]});}
            var Q8;
            {var subQ1=sQuery(id+"F24.wireOp",EDGE,"E45.19.0");Q8=makeQuery(id+"F24.imprint","IMPRINT",FACE,{"disambiguationData":[TD([[makeQuery(id+"F24.imprint","IMPRINT",EDGE,{"derivedFrom":subQ1}),1.0]])]});}
            var Q9;
            {var subQ1=sQuery(id+"F24.wireOp",EDGE,"E45.18.0");Q9=makeQuery(id+"F24.imprint","IMPRINT",FACE,{"disambiguationData":[TD([[makeQuery(id+"F24.imprint","IMPRINT",EDGE,{"derivedFrom":subQ1}),1.0]])]});}
            var Q10;
            {var subQ1=sQuery(id+"F24.wireOp",EDGE,"E45.17.0");Q10=makeQuery(id+"F24.imprint","IMPRINT",FACE,{"disambiguationData":[TD([[makeQuery(id+"F24.imprint","IMPRINT",EDGE,{"derivedFrom":subQ1}),1.0]])]});}
            var Q11;
            {var subQ1=sQuery(id+"F24.wireOp",EDGE,"E45.16.0");Q11=makeQuery(id+"F24.imprint","IMPRINT",FACE,{"disambiguationData":[TD([[makeQuery(id+"F24.imprint","IMPRINT",EDGE,{"derivedFrom":subQ1}),1.0]])]});}
            var Q12;
            {var subQ1=sQuery(id+"F24.wireOp",EDGE,"E45.15.0");Q12=makeQuery(id+"F24.imprint","IMPRINT",FACE,{"disambiguationData":[TD([[makeQuery(id+"F24.imprint","IMPRINT",EDGE,{"derivedFrom":subQ1}),1.0]])]});}
            var Q13;
            {var subQ1=sQuery(id+"F24.wireOp",EDGE,"E45.14.0");Q13=makeQuery(id+"F24.imprint","IMPRINT",FACE,{"disambiguationData":[TD([[makeQuery(id+"F24.imprint","IMPRINT",EDGE,{"derivedFrom":subQ1}),1.0]])]});}
            var Q14;
            {var subQ1=sQuery(id+"F24.wireOp",EDGE,"E45.13.0");Q14=makeQuery(id+"F24.imprint","IMPRINT",FACE,{"disambiguationData":[TD([[makeQuery(id+"F24.imprint","IMPRINT",EDGE,{"derivedFrom":subQ1}),1.0]])]});}
            var Q15;
            {var subQ1=sQuery(id+"F24.wireOp",EDGE,"E45.12.0");Q15=makeQuery(id+"F24.imprint","IMPRINT",FACE,{"disambiguationData":[TD([[makeQuery(id+"F24.imprint","IMPRINT",EDGE,{"derivedFrom":subQ1}),1.0]])]});}
            var Q16;
            {var subQ1=sQuery(id+"F24.wireOp",EDGE,"E45.11.0");Q16=makeQuery(id+"F24.imprint","IMPRINT",FACE,{"disambiguationData":[TD([[makeQuery(id+"F24.imprint","IMPRINT",EDGE,{"derivedFrom":subQ1}),1.0]])]});}
            var Q17;
            {var subQ1=sQuery(id+"F24.wireOp",EDGE,"E45.10.0");Q17=makeQuery(id+"F24.imprint","IMPRINT",FACE,{"disambiguationData":[TD([[makeQuery(id+"F24.imprint","IMPRINT",EDGE,{"derivedFrom":subQ1}),1.0]])]});}
            var Q18;
            {var subQ1=sQuery(id+"F24.wireOp",EDGE,"E45.9.0");Q18=makeQuery(id+"F24.imprint","IMPRINT",FACE,{"disambiguationData":[TD([[makeQuery(id+"F24.imprint","IMPRINT",EDGE,{"derivedFrom":subQ1}),1.0]])]});}
            var Q19;
            {var subQ1=sQuery(id+"F24.wireOp",EDGE,"E45.8.0");Q19=makeQuery(id+"F24.imprint","IMPRINT",FACE,{"disambiguationData":[TD([[makeQuery(id+"F24.imprint","IMPRINT",EDGE,{"derivedFrom":subQ1}),1.0]])]});}
            var Q20;
            {var subQ1=sQuery(id+"F24.wireOp",EDGE,"E45.7.0");Q20=makeQuery(id+"F24.imprint","IMPRINT",FACE,{"disambiguationData":[TD([[makeQuery(id+"F24.imprint","IMPRINT",EDGE,{"derivedFrom":subQ1}),1.0]])]});}
            var Q21;
            {var subQ1=sQuery(id+"F24.wireOp",EDGE,"E45.6.0");Q21=makeQuery(id+"F24.imprint","IMPRINT",FACE,{"disambiguationData":[TD([[makeQuery(id+"F24.imprint","IMPRINT",EDGE,{"derivedFrom":subQ1}),1.0]])]});}
            var Q22;
            {var subQ1=sQuery(id+"F24.wireOp",EDGE,"E45.5.0");Q22=makeQuery(id+"F24.imprint","IMPRINT",FACE,{"disambiguationData":[TD([[makeQuery(id+"F24.imprint","IMPRINT",EDGE,{"derivedFrom":subQ1}),1.0]])]});}
            var Q23;
            {var subQ1=sQuery(id+"F24.wireOp",EDGE,"E45.4.0");Q23=makeQuery(id+"F24.imprint","IMPRINT",FACE,{"disambiguationData":[TD([[makeQuery(id+"F24.imprint","IMPRINT",EDGE,{"derivedFrom":subQ1}),1.0]])]});}
            var Q24;
            {var subQ1=sQuery(id+"F24.wireOp",EDGE,"E45.3.0");Q24=makeQuery(id+"F24.imprint","IMPRINT",FACE,{"disambiguationData":[TD([[makeQuery(id+"F24.imprint","IMPRINT",EDGE,{"derivedFrom":subQ1}),1.0]])]});}
            var Q25;
            {var subQ1=sQuery(id+"F24.wireOp",EDGE,"E45.2.0");Q25=makeQuery(id+"F24.imprint","IMPRINT",FACE,{"disambiguationData":[TD([[makeQuery(id+"F24.imprint","IMPRINT",EDGE,{"derivedFrom":subQ1}),1.0]])]});}
            var Q26;
            Q26=makeQuery(id+"F24.imprint","IMPRINT",FACE,{"disambiguationData":[TD([[makeQuery(id+"F24.imprint","IMPRINT",EDGE,{"derivedFrom":makeQuery(id+"F18.opExtrude","CAP_EDGE",EDGE,{"disambiguationData":[OSD([sQuery(id+"F13.wireOp",EDGE,"E16")])],"isStart":false})}),-1.0]])]});
            extrude(context, id + "F25", {"entities" : qUnion([Q0, Q1, Q2, Q3, Q4, Q5, Q6, Q7, Q8, Q9, Q10, Q11, Q12, Q13, Q14, Q15, Q16, Q17, Q18, Q19, Q20, Q21, Q22, Q23, Q24, Q25, Q26]), "depth" : 4 * mm});
        }
        {
            var Q0;
            Q0=qCreatedBy(makeId("Front.planeOp"),FACE);
            var sketch = newSketch(context, id + "F26", { "sketchPlane" : qUnion([Q0])});
            skLineSegment(sketch, "E46.0", {"start": v(-71, -17) * mm, "end": v(-71, 17) * mm});
            skLineSegment(sketch, "E46.1", {"start": v(-71, -14.5) * mm, "end": v(-71, 14.5) * mm});
            skLineSegment(sketch, "E46.2", {"start": v(-71, -15.75) * mm, "end": v(-71, 15.75) * mm});
            skLineSegment(sketch, "E47.bottom", {"start": v(-71, 14.5) * mm, "end": v(-75, 14.5) * mm});
            skLineSegment(sketch, "E47.top", {"start": v(-71, 17) * mm, "end": v(-75, 17) * mm});
            skLineSegment(sketch, "E47.left", {"start": v(-71, 14.5) * mm, "end": v(-71, 17) * mm});
            skLineSegment(sketch, "E47.right", {"start": v(-75, 14.5) * mm, "end": v(-75, 17) * mm});
            skLineSegment(sketch, "E48", {"start": v(-71, 15.75) * mm, "end": v(-75, 15.75) * mm, "construction": true});
            skLineSegment(sketch, "E49", {"start": v(-73, 17) * mm, "end": v(-73, 15.75) * mm, "construction": true});
            skLineSegment(sketch, "E50", {"start": v(-71, 14.5) * mm, "end": v(-81, 14.5) * mm, "construction": true});
            skArc(sketch, "E51", {"start": v(-71, 15.75) * mm, "mid": v(-71.1, 16.38) * mm, "end": v(-71.24, 17) * mm});
            skArc(sketch, "E52.0.MirrorCS", {"start": v(-75, 15.75) * mm, "mid": v(-74.9, 16.38) * mm, "end": v(-74.76, 17) * mm});
            skLineSegment(sketch, "E53", {"start": v(-71, 0) * mm, "end": v(-77.28, 0) * mm, "construction": true});
            skSolve(sketch);
        }
        {
            var Q0;
            {var subQ0=sQuery(id+"F26.wireOp",EDGE,"E51");Q0=makeQuery(id+"F26.imprint","IMPRINT",FACE,{"disambiguationData":[TD([[makeQuery(id+"F26.imprint","IMPRINT",EDGE,{"derivedFrom":subQ0}),-1.0]])]});}
            var Q1;
            {var subQ0=sQuery(id+"F26.wireOp",EDGE,"E52.0.MirrorCS");Q1=makeQuery(id+"F26.imprint","IMPRINT",FACE,{"disambiguationData":[TD([[makeQuery(id+"F26.imprint","IMPRINT",EDGE,{"derivedFrom":subQ0}),1.0]])]});}
            var Q2;
            Q2=sQuery(id+"F26.wireOp",EDGE,"E53");
            revolve(context, id + "F27", {"operationType" : NewBodyOperationType.REMOVE, "entities" : qUnion([Q0, Q1]), "axis" : qUnion([Q2]), "revolveType" : RevolveType.FULL, "oppositeDirection" : true});
        }
        {
            var Q0;
            Q0=makeQuery(id+"F2.boolean.opBoolean","MERGE",FACE,{"derivedFrom":[makeQuery(id+"F1.opExtrude","CAP_FACE",FACE,{"disambiguationData":[OSD([sQuery(id+"F0.wireOp",EDGE,"E1")])],"isStart":true}),makeQuery(id+"F2.opExtrude","CAP_FACE",FACE,{"disambiguationData":[OSD([sQuery(id+"F0.wireOp",EDGE,"E0"),sQuery(id+"F0.wireOp",EDGE,"E2")])],"isStart":true})]});
            var sketch = newSketch(context, id + "F28", { "sketchPlane" : qUnion([Q0])});
            skCircle(sketch, "E54", {"center": v(0, 0) * mm, "radius": 7 * mm});
            skSolve(sketch);
        }
        {
            var Q0;
            Q0=makeQuery(id+"F28.imprint","IMPRINT",FACE,{"disambiguationData":[TD([[makeQuery(id+"F28.imprint","IMPRINT",EDGE,{"derivedFrom":sQuery(id+"F28.wireOp",EDGE,"E54")}),1.0]])]});
            var Q1;
            Q1=makeQuery(id+"F28.imprint","IMPRINT",FACE,{"disambiguationData":[TD([[makeQuery(id+"F28.imprint","IMPRINT",EDGE,{"derivedFrom":makeQuery(id+"F2.opExtrude","CAP_EDGE",EDGE,{"disambiguationData":[OSD([sQuery(id+"F0.wireOp",EDGE,"E2")])],"isStart":true})}),1.0]])]});
            extrude(context, id + "F29", {"entities" : qUnion([Q0, Q1]), "depth" : 5 * mm});
        }
        {
            var Q0;
            Q0=qCreatedBy(makeId("Top.planeOp"),FACE);
            var sketch = newSketch(context, id + "F30", { "sketchPlane" : qUnion([Q0])});
            skLineSegment(sketch, "E55.0", {"start": v(0, 7) * mm, "end": v(0, -7) * mm});
            skLineSegment(sketch, "E55.1", {"start": v(5, 7) * mm, "end": v(5, -7) * mm});
            skLineSegment(sketch, "E56", {"start": v(0, 0) * mm, "end": v(5, 0) * mm, "construction": true});
            skCircle(sketch, "E57", {"center": v(2.5, 0) * mm, "radius": 1.5 * mm});
            skSolve(sketch);
        }
        {
            var Q0;
            Q0=makeQuery(id+"F30.imprint","IMPRINT",FACE,{"disambiguationData":[TD([[makeQuery(id+"F30.imprint","IMPRINT",EDGE,{"derivedFrom":sQuery(id+"F30.wireOp",EDGE,"E57")}),1.0]])]});
            extrude(context, id + "F31", {"entities" : qUnion([Q0]), "operationType" : NewBodyOperationType.REMOVE, "oppositeDirection" : true, "depth" : 7 * mm});
        }
        {
            var Q0;
            Q0=makeQuery(id+"F29.opExtrude","CAP_FACE",FACE,{"disambiguationData":[OSD([sQuery(id+"F0.wireOp",EDGE,"E1"),sQuery(id+"F28.wireOp",EDGE,"E54")])],"isStart":false});
            var sketch = newSketch(context, id + "F32", { "sketchPlane" : qUnion([Q0])});
            skCircle(sketch, "E58", {"center": v(0, 0) * mm, "radius": 11.5 * mm});
            skCircle(sketch, "E59", {"center": v(0, 0) * mm, "radius": 14 * mm});
            skCircle(sketch, "E60", {"center": v(0, 0) * mm, "radius": 12.75 * mm, "construction": true});
            skLineSegment(sketch, "E61", {"start": v(0, 0) * mm, "end": v(0, 14) * mm, "construction": true});
            skLineSegment(sketch, "E62", {"start": v(0, 0) * mm, "end": v(-1, 12.71) * mm, "construction": true});
            skLineSegment(sketch, "E63", {"start": v(0, 11.5) * mm, "end": v(15, 11.5) * mm, "construction": true});
            skArc(sketch, "E64", {"start": v(-0.85, 13.97) * mm, "mid": v(-1, 12.72) * mm, "end": v(-1.05, 11.45) * mm});
            skArc(sketch, "E65.0.MirrorCS", {"start": v(0.85, 13.97) * mm, "mid": v(1, 12.72) * mm, "end": v(1.05, 11.45) * mm});
            skArc(sketch, "E66.1.0", {"start": v(-3.5, 13.55) * mm, "mid": v(-2.98, 12.4) * mm, "end": v(-2.54, 11.22) * mm});
            skArc(sketch, "E66.1.1", {"start": v(-5.13, 13.03) * mm, "mid": v(-4.88, 11.79) * mm, "end": v(-4.53, 10.57) * mm});
            skArc(sketch, "E66.2.0", {"start": v(-7.52, 11.8) * mm, "mid": v(-6.67, 10.88) * mm, "end": v(-5.89, 9.88) * mm});
            skArc(sketch, "E66.2.1", {"start": v(-8.9, 10.8) * mm, "mid": v(-8.28, 9.7) * mm, "end": v(-7.58, 8.65) * mm});
            skArc(sketch, "E66.3.0", {"start": v(-10.8, 8.9) * mm, "mid": v(-9.7, 8.28) * mm, "end": v(-8.65, 7.58) * mm});
            skArc(sketch, "E66.3.1", {"start": v(-11.8, 7.52) * mm, "mid": v(-10.88, 6.67) * mm, "end": v(-9.88, 5.89) * mm});
            skArc(sketch, "E66.4.0", {"start": v(-13.03, 5.13) * mm, "mid": v(-11.79, 4.88) * mm, "end": v(-10.57, 4.53) * mm});
            skArc(sketch, "E66.4.1", {"start": v(-13.55, 3.5) * mm, "mid": v(-12.4, 2.98) * mm, "end": v(-11.22, 2.54) * mm});
            skArc(sketch, "E66.5.0", {"start": v(-13.97, 0.85) * mm, "mid": v(-12.72, 1) * mm, "end": v(-11.45, 1.05) * mm});
            skArc(sketch, "E66.5.1", {"start": v(-13.97, -0.85) * mm, "mid": v(-12.72, -1) * mm, "end": v(-11.45, -1.05) * mm});
            skArc(sketch, "E66.6.0", {"start": v(-13.55, -3.5) * mm, "mid": v(-12.4, -2.98) * mm, "end": v(-11.22, -2.54) * mm});
            skArc(sketch, "E66.6.1", {"start": v(-13.03, -5.13) * mm, "mid": v(-11.79, -4.88) * mm, "end": v(-10.57, -4.53) * mm});
            skArc(sketch, "E66.7.0", {"start": v(-11.8, -7.52) * mm, "mid": v(-10.88, -6.67) * mm, "end": v(-9.88, -5.89) * mm});
            skArc(sketch, "E66.7.1", {"start": v(-10.8, -8.9) * mm, "mid": v(-9.7, -8.28) * mm, "end": v(-8.65, -7.58) * mm});
            skArc(sketch, "E66.8.0", {"start": v(-8.9, -10.8) * mm, "mid": v(-8.28, -9.7) * mm, "end": v(-7.58, -8.65) * mm});
            skArc(sketch, "E66.8.1", {"start": v(-7.52, -11.8) * mm, "mid": v(-6.67, -10.88) * mm, "end": v(-5.89, -9.88) * mm});
            skArc(sketch, "E66.9.0", {"start": v(-5.13, -13.03) * mm, "mid": v(-4.88, -11.79) * mm, "end": v(-4.53, -10.57) * mm});
            skArc(sketch, "E66.9.1", {"start": v(-3.5, -13.55) * mm, "mid": v(-2.98, -12.4) * mm, "end": v(-2.54, -11.22) * mm});
            skArc(sketch, "E66.10.0", {"start": v(-0.85, -13.97) * mm, "mid": v(-1, -12.72) * mm, "end": v(-1.05, -11.45) * mm});
            skArc(sketch, "E66.10.1", {"start": v(0.85, -13.97) * mm, "mid": v(1, -12.72) * mm, "end": v(1.05, -11.45) * mm});
            skArc(sketch, "E66.11.0", {"start": v(3.5, -13.55) * mm, "mid": v(2.98, -12.4) * mm, "end": v(2.54, -11.22) * mm});
            skArc(sketch, "E66.11.1", {"start": v(5.13, -13.03) * mm, "mid": v(4.88, -11.79) * mm, "end": v(4.53, -10.57) * mm});
            skArc(sketch, "E66.12.0", {"start": v(7.52, -11.8) * mm, "mid": v(6.67, -10.88) * mm, "end": v(5.89, -9.88) * mm});
            skArc(sketch, "E66.12.1", {"start": v(8.9, -10.8) * mm, "mid": v(8.28, -9.7) * mm, "end": v(7.58, -8.65) * mm});
            skArc(sketch, "E66.13.0", {"start": v(10.8, -8.9) * mm, "mid": v(9.7, -8.28) * mm, "end": v(8.65, -7.58) * mm});
            skArc(sketch, "E66.13.1", {"start": v(11.8, -7.52) * mm, "mid": v(10.88, -6.67) * mm, "end": v(9.88, -5.89) * mm});
            skArc(sketch, "E66.14.0", {"start": v(13.03, -5.13) * mm, "mid": v(11.79, -4.88) * mm, "end": v(10.57, -4.53) * mm});
            skArc(sketch, "E66.14.1", {"start": v(13.55, -3.5) * mm, "mid": v(12.4, -2.98) * mm, "end": v(11.22, -2.54) * mm});
            skArc(sketch, "E66.15.0", {"start": v(13.97, -0.85) * mm, "mid": v(12.72, -1) * mm, "end": v(11.45, -1.05) * mm});
            skArc(sketch, "E66.15.1", {"start": v(13.97, 0.85) * mm, "mid": v(12.72, 1) * mm, "end": v(11.45, 1.05) * mm});
            skArc(sketch, "E66.16.0", {"start": v(13.55, 3.5) * mm, "mid": v(12.4, 2.98) * mm, "end": v(11.22, 2.54) * mm});
            skArc(sketch, "E66.16.1", {"start": v(13.03, 5.13) * mm, "mid": v(11.79, 4.88) * mm, "end": v(10.57, 4.53) * mm});
            skArc(sketch, "E66.17.0", {"start": v(11.8, 7.52) * mm, "mid": v(10.88, 6.67) * mm, "end": v(9.88, 5.89) * mm});
            skArc(sketch, "E66.17.1", {"start": v(10.8, 8.9) * mm, "mid": v(9.7, 8.28) * mm, "end": v(8.65, 7.58) * mm});
            skArc(sketch, "E66.18.0", {"start": v(8.9, 10.8) * mm, "mid": v(8.28, 9.7) * mm, "end": v(7.58, 8.65) * mm});
            skArc(sketch, "E66.18.1", {"start": v(7.52, 11.8) * mm, "mid": v(6.67, 10.88) * mm, "end": v(5.89, 9.88) * mm});
            skArc(sketch, "E66.19.0", {"start": v(5.13, 13.03) * mm, "mid": v(4.88, 11.79) * mm, "end": v(4.53, 10.57) * mm});
            skArc(sketch, "E66.19.1", {"start": v(3.5, 13.55) * mm, "mid": v(2.98, 12.4) * mm, "end": v(2.54, 11.22) * mm});
            skSolve(sketch);
        }
        {
            var Q0;
            Q0=makeQuery(id+"F32.imprint","IMPRINT",FACE,{"disambiguationData":[TD([[makeQuery(id+"F32.imprint","IMPRINT",EDGE,{"derivedFrom":makeQuery(id+"F29.opExtrude","CAP_EDGE",EDGE,{"disambiguationData":[OSD([sQuery(id+"F28.wireOp",EDGE,"E54")])],"isStart":false})}),-1.0]])]});
            var Q1;
            Q1=makeQuery(id+"F32.imprint","IMPRINT",FACE,{"disambiguationData":[TD([[makeQuery(id+"F32.imprint","IMPRINT",EDGE,{"derivedFrom":makeQuery(id+"F29.opExtrude","CAP_EDGE",EDGE,{"disambiguationData":[OSD([sQuery(id+"F28.wireOp",EDGE,"E54")])],"isStart":false})}),1.0]])]});
            var Q2;
            {var subQ0=sQuery(id+"F32.wireOp",EDGE,"E66.2.0");Q2=makeQuery(id+"F32.imprint","IMPRINT",FACE,{"disambiguationData":[TD([[makeQuery(id+"F32.imprint","IMPRINT",EDGE,{"derivedFrom":subQ0}),-1.0]])]});}
            var Q3;
            {var subQ1=sQuery(id+"F32.wireOp",EDGE,"E66.1.0");Q3=makeQuery(id+"F32.imprint","IMPRINT",FACE,{"disambiguationData":[TD([[makeQuery(id+"F32.imprint","IMPRINT",EDGE,{"derivedFrom":subQ1}),-1.0]])]});}
            var Q4;
            {var subQ1=sQuery(id+"F32.wireOp",EDGE,"E64");Q4=makeQuery(id+"F32.imprint","IMPRINT",FACE,{"disambiguationData":[TD([[makeQuery(id+"F32.imprint","IMPRINT",EDGE,{"derivedFrom":subQ1}),1.0]])]});}
            var Q5;
            {var subQ1=sQuery(id+"F32.wireOp",EDGE,"E66.19.0");Q5=makeQuery(id+"F32.imprint","IMPRINT",FACE,{"disambiguationData":[TD([[makeQuery(id+"F32.imprint","IMPRINT",EDGE,{"derivedFrom":subQ1}),-1.0]])]});}
            var Q6;
            {var subQ0=sQuery(id+"F32.wireOp",EDGE,"E66.18.0");Q6=makeQuery(id+"F32.imprint","IMPRINT",FACE,{"disambiguationData":[TD([[makeQuery(id+"F32.imprint","IMPRINT",EDGE,{"derivedFrom":subQ0}),-1.0]])]});}
            var Q7;
            {var subQ0=sQuery(id+"F32.wireOp",EDGE,"E66.17.0");Q7=makeQuery(id+"F32.imprint","IMPRINT",FACE,{"disambiguationData":[TD([[makeQuery(id+"F32.imprint","IMPRINT",EDGE,{"derivedFrom":subQ0}),-1.0]])]});}
            var Q8;
            {var subQ1=sQuery(id+"F32.wireOp",EDGE,"E66.16.0");Q8=makeQuery(id+"F32.imprint","IMPRINT",FACE,{"disambiguationData":[TD([[makeQuery(id+"F32.imprint","IMPRINT",EDGE,{"derivedFrom":subQ1}),-1.0]])]});}
            var Q9;
            {var subQ2=sQuery(id+"F32.wireOp",EDGE,"E66.15.0");Q9=makeQuery(id+"F32.imprint","IMPRINT",FACE,{"disambiguationData":[TD([[makeQuery(id+"F32.imprint","IMPRINT",EDGE,{"derivedFrom":subQ2}),-1.0]])]});}
            var Q10;
            {var subQ1=sQuery(id+"F32.wireOp",EDGE,"E66.14.0");Q10=makeQuery(id+"F32.imprint","IMPRINT",FACE,{"disambiguationData":[TD([[makeQuery(id+"F32.imprint","IMPRINT",EDGE,{"derivedFrom":subQ1}),-1.0]])]});}
            var Q11;
            {var subQ0=sQuery(id+"F32.wireOp",EDGE,"E66.13.0");Q11=makeQuery(id+"F32.imprint","IMPRINT",FACE,{"disambiguationData":[TD([[makeQuery(id+"F32.imprint","IMPRINT",EDGE,{"derivedFrom":subQ0}),-1.0]])]});}
            var Q12;
            {var subQ2=sQuery(id+"F32.wireOp",EDGE,"E66.12.0");Q12=makeQuery(id+"F32.imprint","IMPRINT",FACE,{"disambiguationData":[TD([[makeQuery(id+"F32.imprint","IMPRINT",EDGE,{"derivedFrom":subQ2}),-1.0]])]});}
            var Q13;
            {var subQ2=sQuery(id+"F32.wireOp",EDGE,"E66.11.0");Q13=makeQuery(id+"F32.imprint","IMPRINT",FACE,{"disambiguationData":[TD([[makeQuery(id+"F32.imprint","IMPRINT",EDGE,{"derivedFrom":subQ2}),-1.0]])]});}
            var Q14;
            {var subQ1=sQuery(id+"F32.wireOp",EDGE,"E66.10.0");Q14=makeQuery(id+"F32.imprint","IMPRINT",FACE,{"disambiguationData":[TD([[makeQuery(id+"F32.imprint","IMPRINT",EDGE,{"derivedFrom":subQ1}),-1.0]])]});}
            var Q15;
            {var subQ0=sQuery(id+"F32.wireOp",EDGE,"E66.9.0");Q15=makeQuery(id+"F32.imprint","IMPRINT",FACE,{"disambiguationData":[TD([[makeQuery(id+"F32.imprint","IMPRINT",EDGE,{"derivedFrom":subQ0}),-1.0]])]});}
            var Q16;
            {var subQ2=sQuery(id+"F32.wireOp",EDGE,"E66.8.0");Q16=makeQuery(id+"F32.imprint","IMPRINT",FACE,{"disambiguationData":[TD([[makeQuery(id+"F32.imprint","IMPRINT",EDGE,{"derivedFrom":subQ2}),-1.0]])]});}
            var Q17;
            {var subQ1=sQuery(id+"F32.wireOp",EDGE,"E66.7.0");Q17=makeQuery(id+"F32.imprint","IMPRINT",FACE,{"disambiguationData":[TD([[makeQuery(id+"F32.imprint","IMPRINT",EDGE,{"derivedFrom":subQ1}),-1.0]])]});}
            var Q18;
            {var subQ1=sQuery(id+"F32.wireOp",EDGE,"E66.6.0");Q18=makeQuery(id+"F32.imprint","IMPRINT",FACE,{"disambiguationData":[TD([[makeQuery(id+"F32.imprint","IMPRINT",EDGE,{"derivedFrom":subQ1}),-1.0]])]});}
            var Q19;
            {var subQ1=sQuery(id+"F32.wireOp",EDGE,"E66.5.0");Q19=makeQuery(id+"F32.imprint","IMPRINT",FACE,{"disambiguationData":[TD([[makeQuery(id+"F32.imprint","IMPRINT",EDGE,{"derivedFrom":subQ1}),-1.0]])]});}
            var Q20;
            {var subQ1=sQuery(id+"F32.wireOp",EDGE,"E66.4.0");Q20=makeQuery(id+"F32.imprint","IMPRINT",FACE,{"disambiguationData":[TD([[makeQuery(id+"F32.imprint","IMPRINT",EDGE,{"derivedFrom":subQ1}),-1.0]])]});}
            var Q21;
            {var subQ0=sQuery(id+"F32.wireOp",EDGE,"E66.3.0");Q21=makeQuery(id+"F32.imprint","IMPRINT",FACE,{"disambiguationData":[TD([[makeQuery(id+"F32.imprint","IMPRINT",EDGE,{"derivedFrom":subQ0}),-1.0]])]});}
            extrude(context, id + "F33", {"entities" : qUnion([Q0, Q1, Q2, Q3, Q4, Q5, Q6, Q7, Q8, Q9, Q10, Q11, Q12, Q13, Q14, Q15, Q16, Q17, Q18, Q19, Q20, Q21]), "depth" : 5 * mm});
        }
        {
            var Q0;
            Q0=qCreatedBy(makeId("Front.planeOp"),FACE);
            var sketch = newSketch(context, id + "F34", { "sketchPlane" : qUnion([Q0])});
            skLineSegment(sketch, "E67.0", {"start": v(5, 11.5) * mm, "end": v(5, -11.5) * mm});
            skLineSegment(sketch, "E67.1", {"start": v(5, 12.75) * mm, "end": v(5, -12.75) * mm});
            skLineSegment(sketch, "E67.2", {"start": v(5, 14) * mm, "end": v(5, -14) * mm});
            skLineSegment(sketch, "E68.bottom", {"start": v(5, 11.5) * mm, "end": v(10, 11.5) * mm});
            skLineSegment(sketch, "E68.top", {"start": v(5, 14) * mm, "end": v(10, 14) * mm});
            skLineSegment(sketch, "E68.left", {"start": v(5, 11.5) * mm, "end": v(5, 14) * mm});
            skLineSegment(sketch, "E68.right", {"start": v(10, 11.5) * mm, "end": v(10, 14) * mm});
            skLineSegment(sketch, "E69", {"start": v(7.5, 14) * mm, "end": v(7.5, 11.5) * mm, "construction": true});
            skLineSegment(sketch, "E70", {"start": v(5, 11.5) * mm, "end": v(15, 11.5) * mm, "construction": true});
            skArc(sketch, "E71", {"start": v(5.24, 14) * mm, "mid": v(5.1, 13.38) * mm, "end": v(5, 12.75) * mm});
            skArc(sketch, "E72.0.MirrorCS", {"start": v(9.76, 14) * mm, "mid": v(9.9, 13.38) * mm, "end": v(10, 12.75) * mm});
            skLineSegment(sketch, "E73", {"start": v(5, 0) * mm, "end": v(9.68, 0) * mm});
            skSolve(sketch);
        }
        {
            var Q0;
            {var subQ0=sQuery(id+"F34.wireOp",EDGE,"E71");Q0=makeQuery(id+"F34.imprint","IMPRINT",FACE,{"disambiguationData":[TD([[makeQuery(id+"F34.imprint","IMPRINT",EDGE,{"derivedFrom":subQ0}),-1.0]])]});}
            var Q1;
            {var subQ0=sQuery(id+"F34.wireOp",EDGE,"E72.0.MirrorCS");Q1=makeQuery(id+"F34.imprint","IMPRINT",FACE,{"disambiguationData":[TD([[makeQuery(id+"F34.imprint","IMPRINT",EDGE,{"derivedFrom":subQ0}),1.0]])]});}
            var Q2;
            Q2=sQuery(id+"F34.wireOp",EDGE,"E73");
            revolve(context, id + "F35", {"operationType" : NewBodyOperationType.REMOVE, "entities" : qUnion([Q0, Q1]), "axis" : qUnion([Q2]), "revolveType" : RevolveType.FULL, "oppositeDirection" : true});
        }
    });
